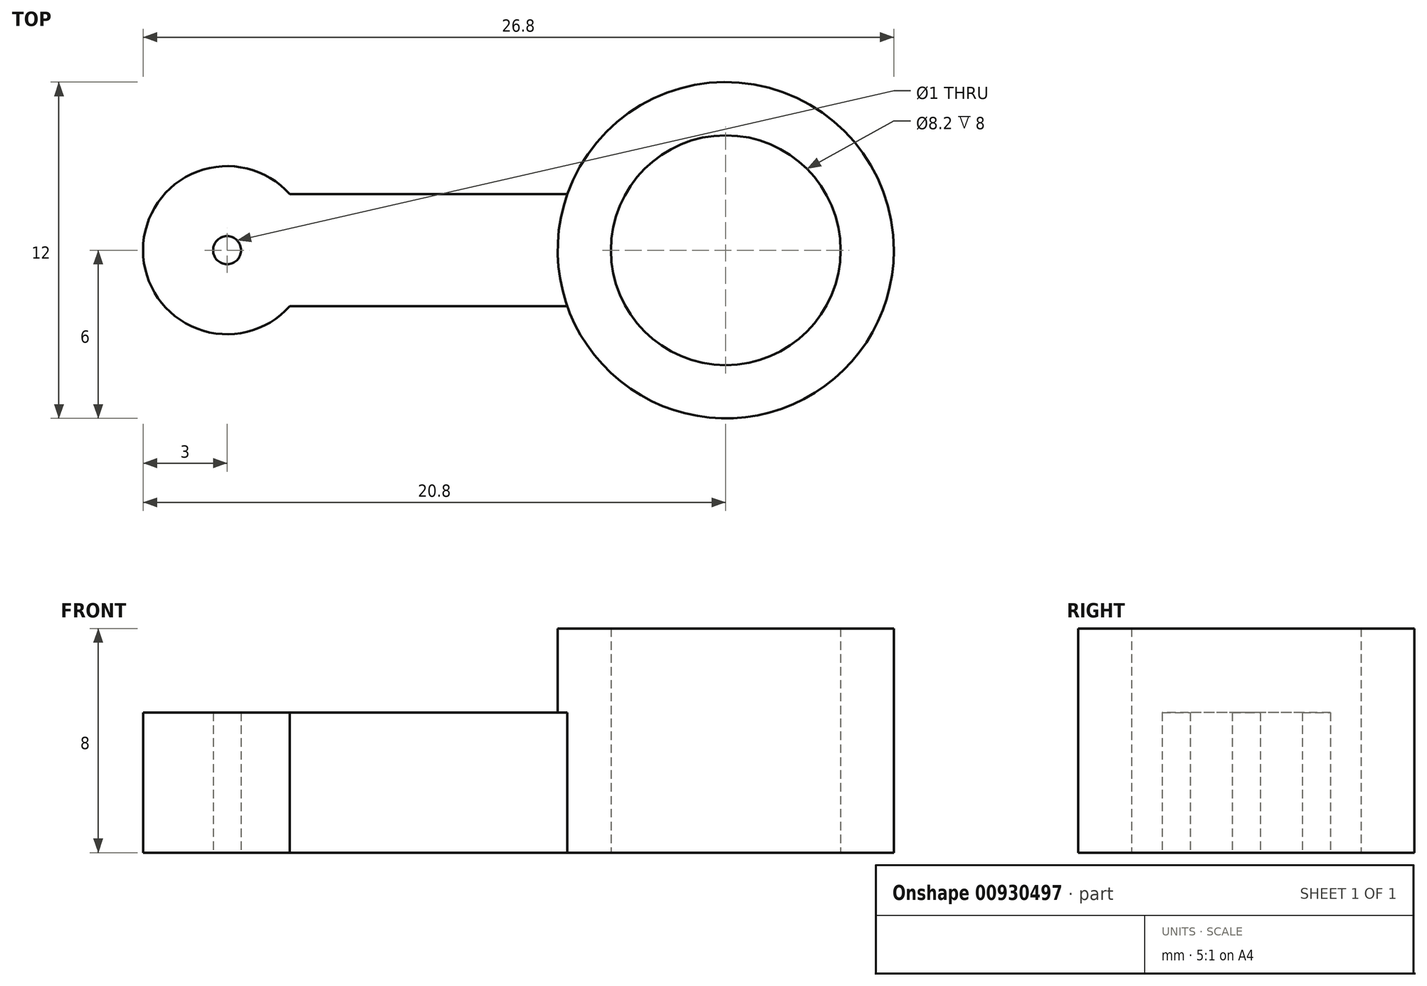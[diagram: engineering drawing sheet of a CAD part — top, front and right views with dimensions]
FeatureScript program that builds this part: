
annotation { "Feature Type Name" : "Feature", "Feature Type Description" : "" }
export const myFeature = defineFeature(function(context is Context, id is Id, definition is map)
    precondition{}
    {
        {
            var Q0;
            Q0=qCreatedBy(makeId("Top.planeOp"),FACE);
            var sketch = newSketch(context, id + "F0", { "sketchPlane" : qUnion([Q0])});
            skLineSegment(sketch, "E0.bottom", {"start": v(-15.56, 2) * mm, "end": v(0, 2) * mm});
            skLineSegment(sketch, "E0.top", {"start": v(-15.56, -2) * mm, "end": v(0, -2) * mm});
            skLineSegment(sketch, "E0.right", {"start": v(0, 2) * mm, "end": v(0, -2) * mm});
            skArc(sketch, "E1", {"start": v(-15.56, 2) * mm, "mid": v(-20.8, 0) * mm, "end": v(-15.56, -2) * mm});
            skLineSegment(sketch, "E2", {"start": v(0, 57.31) * mm, "end": v(0, -56.63) * mm, "construction": true});
            skCircle(sketch, "E3", {"center": v(-17.8, 0) * mm, "radius": 0.5 * mm});
            skSolve(sketch);
        }
        {
            var Q0;
            Q0=qCreatedBy(makeId("Top.planeOp"),FACE);
            var sketch = newSketch(context, id + "F1", { "sketchPlane" : qUnion([Q0])});
            skCircle(sketch, "E4", {"center": v(0, 0) * mm, "radius": 6 * mm});
            skSolve(sketch);
        }
        {
            var Q0;
            Q0 = qSketchRegion(id + "F1", true);
            extrude(context, id + "F2", {"entities" : qUnion([Q0]), "depth" : 8 * mm, "offsetDistance" : 25 * mm});
        }
        {
            var Q0;
            Q0 = qSketchRegion(id + "F0", true);
            extrude(context, id + "F3", {"entities" : qUnion([Q0]), "operationType" : NewBodyOperationType.ADD, "depth" : 5 * mm, "offsetDistance" : 25 * mm});
        }
        {
            var Q0;
            Q0=qCreatedBy(makeId("Top.planeOp"),FACE);
            var sketch = newSketch(context, id + "F4", { "sketchPlane" : qUnion([Q0])});
            skCircle(sketch, "E5", {"center": v(0, 0) * mm, "radius": 4.1 * mm});
            skSolve(sketch);
        }
        {
            var Q0;
            Q0 = qSketchRegion(id + "F4", true);
            extrude(context, id + "F5", {"entities" : qUnion([Q0]), "operationType" : NewBodyOperationType.REMOVE, "endBound" : BoundingType.THROUGH_ALL, "depth" : 25 * mm, "offsetDistance" : 25 * mm});
        }
    });
